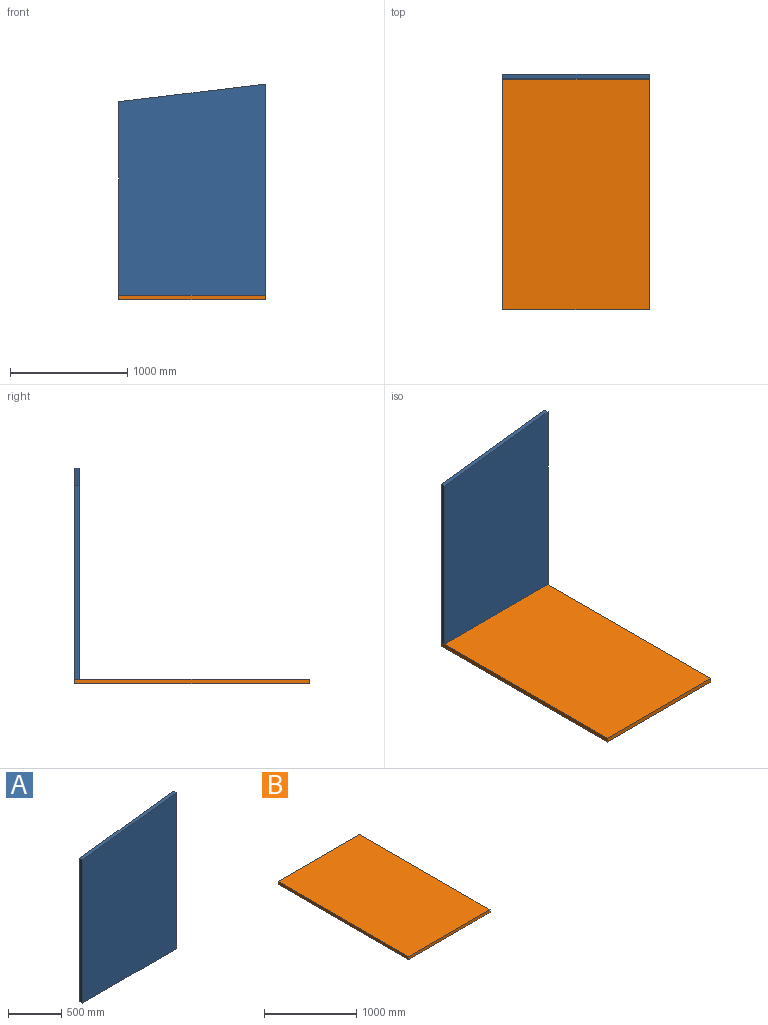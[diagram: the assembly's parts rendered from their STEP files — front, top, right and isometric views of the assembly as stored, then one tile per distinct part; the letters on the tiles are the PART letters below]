
ASSEMBLY  parts=2 mates=1
PART A: 6 faces, bbox 1250x38x1800 mm
  f0: plane 1250x38mm, normal (0,0,-1), area 47500mm2, adj f1,f3,f4,f5
  f1: plane 1800x38mm, normal (1,0,0), area 68400mm2, adj f0,f2,f4,f5
  f2: plane 1250x150mm, normal (-0.12,0,0.99), area 47840.8mm2, adj f1,f3,f4,f5
  f3: plane 1650x38mm, normal (-1,0,0), area 62700mm2, adj f0,f2,f4,f5
  f4: plane 1800x1250mm, normal (0,-1,0), area 2156250mm2, adj f0,f1,f2,f3
  f5: plane 1800x1250mm, normal (0,1,0), area 2156250mm2, adj f0,f1,f2,f3
PART B: 6 faces, bbox 1250x2000x38 mm
  f0: plane 2000x38mm, normal (-1,0,0), area 76000mm2, adj f1,f3,f4,f5
  f1: plane 1250x38mm, normal (0,-1,0), area 47500mm2, adj f0,f2,f4,f5
  f2: plane 2000x38mm, normal (1,0,0), area 76000mm2, adj f1,f3,f4,f5
  f3: plane 1250x38mm, normal (0,1,0), area 47500mm2, adj f0,f2,f4,f5
  f4: plane 2000x1250mm, normal (0,0,1), area 2500000mm2, adj f0,f1,f2,f3
  f5: plane 2000x1250mm, normal (0,0,-1), area 2500000mm2, adj f0,f1,f2,f3
PLACE A t=(-691.59,996.98,1645.91)mm
PLACE B at identity fixed
MATE fastened A.f0 <-> B.f4  axis (0,0,-1) through (522.89,996.98,38)mm
